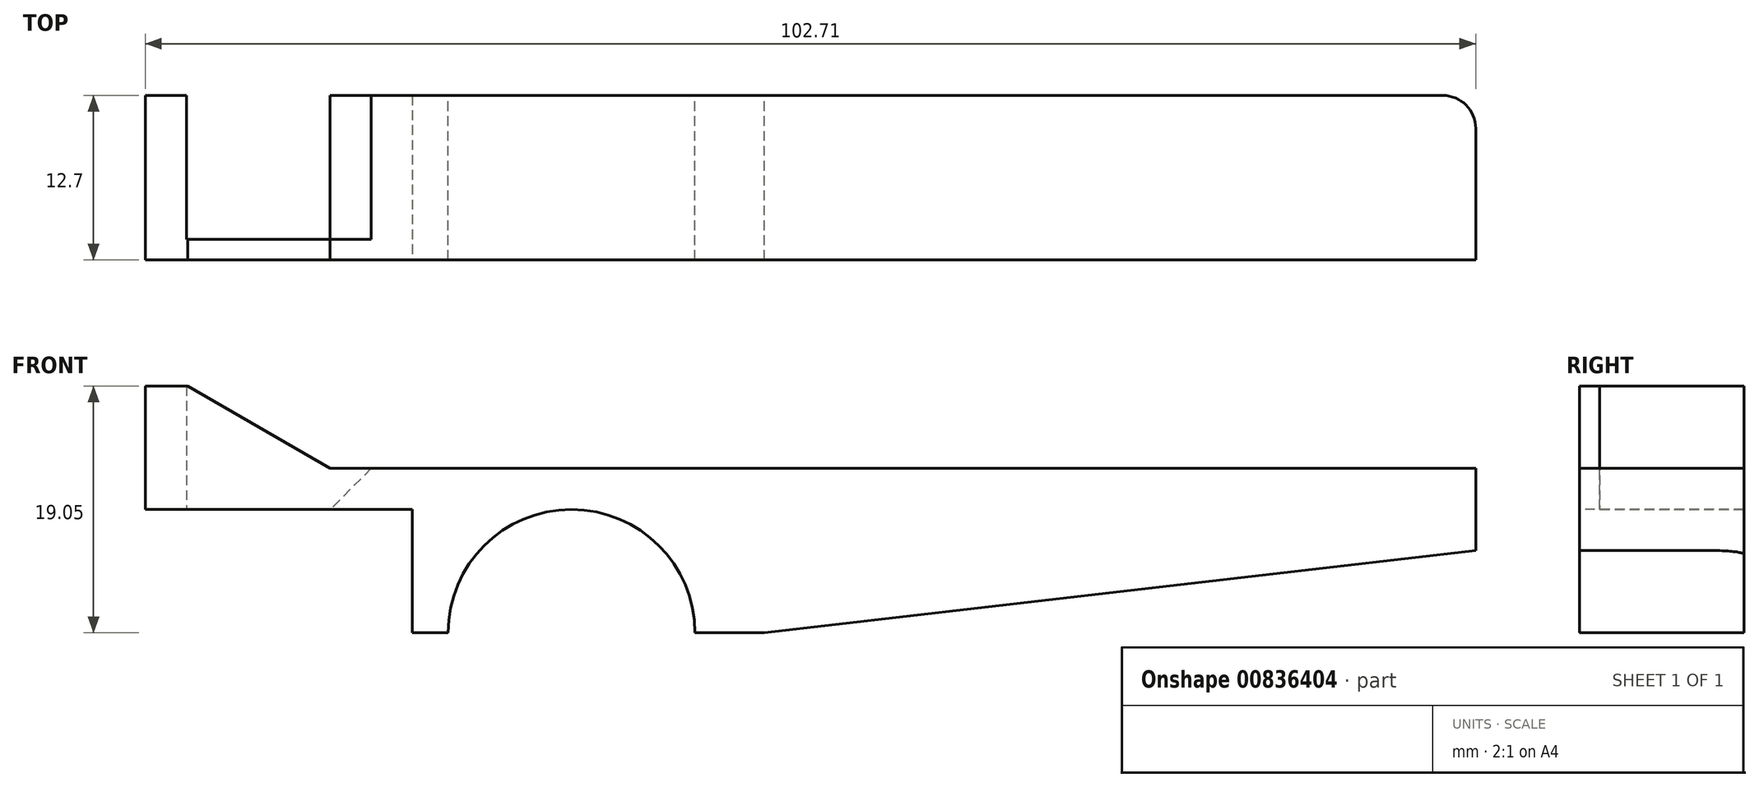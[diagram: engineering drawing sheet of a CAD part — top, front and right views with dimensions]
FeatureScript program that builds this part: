
annotation { "Feature Type Name" : "Feature", "Feature Type Description" : "" }
export const myFeature = defineFeature(function(context is Context, id is Id, definition is map)
    precondition{}
    {
        {
            var Q0;
            Q0=qCreatedBy(makeId("Top.planeOp"),FACE);
            var sketch = newSketch(context, id + "F0", { "sketchPlane" : qUnion([Q0])});
            skLineSegment(sketch, "E0.bottom", {"start": v(-19.03, 12.7) * mm, "end": v(19.07, 12.7) * mm});
            skLineSegment(sketch, "E0.top", {"start": v(-19.03, 0) * mm, "end": v(19.07, 0) * mm});
            skLineSegment(sketch, "E0.left", {"start": v(-19.03, 12.7) * mm, "end": v(-19.03, 0) * mm});
            skLineSegment(sketch, "E0.right", {"start": v(19.07, 12.7) * mm, "end": v(19.07, 0) * mm});
            skLineSegment(sketch, "E1.bottom", {"start": v(-19.03, 12.7) * mm, "end": v(-15.85, 12.7) * mm});
            skLineSegment(sketch, "E1.top", {"start": v(-19.03, 0) * mm, "end": v(-15.85, 0) * mm});
            skLineSegment(sketch, "E1.right", {"start": v(-15.85, 12.7) * mm, "end": v(-15.85, 0) * mm});
            skLineSegment(sketch, "E2.bottom", {"start": v(-15.85, 0) * mm, "end": v(-4.75, 0) * mm});
            skLineSegment(sketch, "E2.top", {"start": v(-15.85, 1.57) * mm, "end": v(-4.75, 1.57) * mm});
            skLineSegment(sketch, "E2.left", {"start": v(-15.85, 0) * mm, "end": v(-15.85, 1.57) * mm});
            skLineSegment(sketch, "E2.right", {"start": v(-4.75, 0) * mm, "end": v(-4.75, 1.57) * mm});
            skLineSegment(sketch, "E3.top", {"start": v(-15.85, 12.7) * mm, "end": v(-4.75, 12.7) * mm});
            skLineSegment(sketch, "E3.left", {"start": v(-15.85, 1.57) * mm, "end": v(-15.85, 12.7) * mm});
            skLineSegment(sketch, "E3.right", {"start": v(-4.75, 1.57) * mm, "end": v(-4.75, 12.7) * mm});
            skSolve(sketch);
        }
        {
            var Q0;
            {var subQ3=sQuery(id+"F0.wireOp",EDGE,"E0.right");Q0=makeQuery(id+"F0.imprint","IMPRINT",FACE,{"disambiguationData":[TD([[makeQuery(id+"F0.imprint","IMPRINT",EDGE,{"derivedFrom":subQ3}),-1.0]])]});}
            var Q1;
            {var subQ4=sQuery(id+"F0.wireOp",EDGE,"E0.left");Q1=makeQuery(id+"F0.imprint","IMPRINT",FACE,{"disambiguationData":[TD([[makeQuery(id+"F0.imprint","IMPRINT",EDGE,{"derivedFrom":subQ4}),1.0]])]});}
            var Q2;
            {var subQ4=sQuery(id+"F0.wireOp",EDGE,"E2.top");Q2=makeQuery(id+"F0.imprint","IMPRINT",FACE,{"disambiguationData":[TD([[makeQuery(id+"F0.imprint","IMPRINT",EDGE,{"derivedFrom":subQ4}),-1.0]])]});}
            extrude(context, id + "F1", {"entities" : qUnion([Q0, Q1, Q2]), "depth" : 12.7 * mm, "offsetDistance" : 25.4 * mm});
        }
        {
            var Q0;
            Q0=makeQuery(id+"F1.opExtrude","CAP_FACE",FACE,{"disambiguationData":[OSD([sQuery(id+"F0.wireOp",EDGE,"E0.bottom"),sQuery(id+"F0.wireOp",EDGE,"E0.top"),sQuery(id+"F0.wireOp",EDGE,"E0.left"),sQuery(id+"F0.wireOp",EDGE,"E0.right"),sQuery(id+"F0.wireOp",EDGE,"E1.right"),sQuery(id+"F0.wireOp",EDGE,"E2.top"),sQuery(id+"F0.wireOp",EDGE,"E3.right")])],"isStart":true});
            var sketch = newSketch(context, id + "F2", { "sketchPlane" : qUnion([Q0])});
            skLineSegment(sketch, "E4", {"start": v(-4.75, -1.57) * mm, "end": v(1.6, -1.57) * mm});
            skLineSegment(sketch, "E5", {"start": v(1.6, -1.57) * mm, "end": v(1.6, 0) * mm});
            skLineSegment(sketch, "E6", {"start": v(1.6, 0) * mm, "end": v(1.6, 0) * mm});
            skLineSegment(sketch, "E7", {"start": v(1.6, 0) * mm, "end": v(1.6, -12.7) * mm});
            skLineSegment(sketch, "E8", {"start": v(1.6, -12.7) * mm, "end": v(-19.03, -12.7) * mm});
            skLineSegment(sketch, "E9", {"start": v(-19.03, -12.7) * mm, "end": v(-19.03, 0) * mm});
            skLineSegment(sketch, "E10", {"start": v(-19.03, 0) * mm, "end": v(1.6, 0) * mm});
            skSolve(sketch);
        }
        {
            var Q0;
            Q0 = qSketchRegion(id + "F2", true);
            extrude(context, id + "F3", {"entities" : qUnion([Q0]), "operationType" : NewBodyOperationType.REMOVE, "oppositeDirection" : true, "depth" : 9.52 * mm, "offsetDistance" : 25.4 * mm});
        }
        {
            var Q0;
            Q0=makeQuery(id+"F1.opExtrude","CAP_FACE",FACE,{"disambiguationData":[OSD([sQuery(id+"F0.wireOp",EDGE,"E0.bottom"),sQuery(id+"F0.wireOp",EDGE,"E0.top"),sQuery(id+"F0.wireOp",EDGE,"E0.left"),sQuery(id+"F0.wireOp",EDGE,"E0.right"),sQuery(id+"F0.wireOp",EDGE,"E1.right"),sQuery(id+"F0.wireOp",EDGE,"E2.top"),sQuery(id+"F0.wireOp",EDGE,"E3.right")])],"isStart":false});
            var sketch = newSketch(context, id + "F4", { "sketchPlane" : qUnion([Q0])});
            skLineSegment(sketch, "E11", {"start": v(-19.03, 12.7) * mm, "end": v(-15.85, 12.7) * mm});
            skLineSegment(sketch, "E12", {"start": v(-15.85, 12.7) * mm, "end": v(-15.85, 1.57) * mm});
            skLineSegment(sketch, "E13", {"start": v(-15.85, 1.57) * mm, "end": v(-4.75, 1.57) * mm});
            skLineSegment(sketch, "E14", {"start": v(-4.75, 1.57) * mm, "end": v(-4.75, 0) * mm});
            skLineSegment(sketch, "E15", {"start": v(-4.75, 0) * mm, "end": v(-19.03, 0) * mm});
            skLineSegment(sketch, "E16", {"start": v(-19.03, 0) * mm, "end": v(-19.03, 12.7) * mm});
            skSolve(sketch);
        }
        {
            var Q0;
            Q0=makeQuery(id+"F4.imprint","IMPRINT",FACE,{"disambiguationData":[TD([[makeQuery(id+"F4.imprint","IMPRINT",EDGE,{"derivedFrom":sQuery(id+"F4.wireOp",EDGE,"E11")}),-1.0]])]});
            extrude(context, id + "F5", {"entities" : qUnion([Q0]), "operationType" : NewBodyOperationType.ADD, "depth" : 6.35 * mm, "offsetDistance" : 25.4 * mm});
        }
        {
            var Q0;
            Q0=makeQuery(id+"F5.opExtrude","CAP_EDGE",EDGE,{"disambiguationData":[OSD([sQuery(id+"F4.wireOp",EDGE,"E14")])],"isStart":false});
            chamfer(context, id + "F6", {"entities" : qUnion([Q0]), "chamferType" : ChamferType.OFFSET_ANGLE, "width" : 6.35 * mm, "oppositeDirection" : false, "angle" : 60 * degree, "tangentPropagation" : true});
        }
        {
            var Q0;
            Q0=makeQuery(id+"F1.opExtrude","CAP_EDGE",EDGE,{"disambiguationData":[OSD([sQuery(id+"F0.wireOp",EDGE,"E3.right")])],"isStart":false});
            chamfer(context, id + "F7", {"entities" : qUnion([Q0]), "width" : 3.17 * mm, "tangentPropagation" : true});
        }
        {
            var Q0;
            Q0=makeQuery(id+"F1.opExtrude","CAP_EDGE",EDGE,{"disambiguationData":[OSD([sQuery(id+"F0.wireOp",EDGE,"E0.right")])],"isStart":false});
            var Q1;
            Q1=makeQuery(id+"F1.opExtrude","CAP_EDGE",EDGE,{"disambiguationData":[OSD([sQuery(id+"F0.wireOp",EDGE,"E0.right")])],"isStart":true});
            var Q2;
            Q2=makeQuery(id+"F1.opExtrude","SWEPT_EDGE",EDGE,{"disambiguationData":[OSD([sQuery(id+"F0.wireOp",EDGE,"E0.bottom"),sQuery(id+"F0.wireOp",EDGE,"E0.right")])]});
            chamfer(context, id + "F8", {"entities" : qUnion([Q0, Q1, Q2]), "width" : 2.54 * mm, "tangentPropagation" : true});
        }
        {
            var Q0;
            Q0=makeQuery(id+"F1.opExtrude","CAP_FACE",FACE,{"disambiguationData":[OSD([sQuery(id+"F0.wireOp",EDGE,"E0.bottom"),sQuery(id+"F0.wireOp",EDGE,"E0.top"),sQuery(id+"F0.wireOp",EDGE,"E0.left"),sQuery(id+"F0.wireOp",EDGE,"E0.right"),sQuery(id+"F0.wireOp",EDGE,"E1.right"),sQuery(id+"F0.wireOp",EDGE,"E2.top"),sQuery(id+"F0.wireOp",EDGE,"E3.right")])],"isStart":false});
            var sketch = newSketch(context, id + "F9", { "sketchPlane" : qUnion([Q0])});
            skLineSegment(sketch, "E17.bottom", {"start": v(7.48, 12.7) * mm, "end": v(22.53, 12.7) * mm});
            skLineSegment(sketch, "E17.top", {"start": v(7.48, 0) * mm, "end": v(22.53, 0) * mm});
            skLineSegment(sketch, "E17.left", {"start": v(7.48, 12.7) * mm, "end": v(7.48, 0) * mm});
            skLineSegment(sketch, "E17.right", {"start": v(22.53, 12.7) * mm, "end": v(22.53, 0) * mm});
            skSolve(sketch);
        }
        {
            var Q0;
            Q0 = qSketchRegion(id + "F9", true);
            extrude(context, id + "F10", {"entities" : qUnion([Q0]), "operationType" : NewBodyOperationType.REMOVE, "oppositeDirection" : true, "depth" : 25.4 * mm, "offsetDistance" : 25.4 * mm});
        }
        {
            var Q0;
            Q0=makeQuery(id+"F10.boolean.opBoolean","COPY",FACE,{"derivedFrom":makeQuery(id+"F10.opExtrude","SWEPT_FACE",FACE,{"disambiguationData":[OSD([sQuery(id+"F9.wireOp",EDGE,"E17.left")])]})});
            extrude(context, id + "F11", {"entities" : qUnion([Q0]), "operationType" : NewBodyOperationType.ADD, "depth" : 76.2 * mm, "offsetDistance" : 25.4 * mm});
        }
        {
            var Q0;
            {var subQ0=sQuery(id+"F0.wireOp",EDGE,"E0.bottom");Q0=makeQuery(id+"F11.boolean.opBoolean","MERGE",FACE,{"derivedFrom":[makeQuery(id+"F1.opExtrude","SWEPT_FACE",FACE,{"disambiguationData":[OSD([subQ0]),TDD([makeQuery(id+"F0.imprint","IMPRINT",EDGE,{"disambiguationData":[TD([[makeQuery(id+"F0.imprint","INTERSECT",VERTEX,{"derivedFrom":[subQ0,sQuery(id+"F0.wireOp",EDGE,"E3.right")]}),-1.0]])],"derivedFrom":subQ0})])]}),makeQuery(id+"F11.opExtrude","SWEPT_FACE",FACE,{"disambiguationData":[OSD([subQ0,sQuery(id+"F9.wireOp",EDGE,"E17.bottom"),sQuery(id+"F9.wireOp",EDGE,"E17.left")])]})]});}
            var sketch = newSketch(context, id + "F12", { "sketchPlane" : qUnion([Q0])});
            skPoint(sketch, "E18", {"position": v(-13.88, 0) * mm});
            skCircle(sketch, "E19", {"center": v(-13.88, 0) * mm, "radius": 9.53 * mm});
            skSolve(sketch);
        }
        {
            var Q0;
            {var subQ0=sQuery(id+"F12.wireOp",EDGE,"E19");var subQ1=sQuery(id+"F9.wireOp",EDGE,"E17.left");var subQ2=sQuery(id+"F0.wireOp",EDGE,"E3.right");var subQ3=sQuery(id+"F0.wireOp",EDGE,"E2.top");var subQ4=sQuery(id+"F0.wireOp",EDGE,"E1.right");var subQ5=sQuery(id+"F0.wireOp",EDGE,"E0.right");var subQ6=sQuery(id+"F0.wireOp",EDGE,"E0.left");var subQ7=sQuery(id+"F0.wireOp",EDGE,"E0.top");var subQ8=sQuery(id+"F0.wireOp",EDGE,"E0.bottom");var subQ9=makeQuery(id+"F11.boolean.opBoolean","MERGE",EDGE,{"derivedFrom":[makeQuery(id+"F1.opExtrude","CAP_EDGE",EDGE,{"disambiguationData":[OSD([subQ8]),TDD([makeQuery(id+"F0.imprint","IMPRINT",EDGE,{"disambiguationData":[TD([[makeQuery(id+"F0.imprint","INTERSECT",VERTEX,{"derivedFrom":[subQ8,subQ2]}),-1.0]])],"derivedFrom":subQ8})])],"isStart":true}),makeQuery(id+"F11.opExtrude","SWEPT_EDGE",EDGE,{"disambiguationData":[OSD([subQ8,subQ7,subQ6,subQ5,subQ4,subQ3,subQ2,subQ1]),TDD([makeQuery(id+"F10.boolean.opBoolean","INTERSECT",VERTEX,{"disambiguationData":[OD(0.0)],"derivedFrom":[makeQuery(id+"F1.opExtrude","CAP_FACE",FACE,{"disambiguationData":[OSD([subQ8,subQ7,subQ6,subQ5,subQ4,subQ3,subQ2])],"isStart":true}),makeQuery(id+"F10.opExtrude","SWEPT_FACE",FACE,{"disambiguationData":[OSD([subQ1])]})]})])]})]});var subQ10=makeQuery(id+"F12.imprint","INTERSECT",VERTEX,{"disambiguationData":[OD(0.0)],"derivedFrom":[subQ9,subQ0]});Q0=makeQuery(id+"F12.imprint","IMPRINT",FACE,{"disambiguationData":[TD([[makeQuery(id+"F12.imprint","IMPRINT",EDGE,{"disambiguationData":[TD([[subQ10,-1.0]])],"derivedFrom":subQ0}),1.0]])]});}
            extrude(context, id + "F13", {"entities" : qUnion([Q0]), "operationType" : NewBodyOperationType.REMOVE, "oppositeDirection" : true, "depth" : 25.4 * mm, "offsetDistance" : 25.4 * mm});
        }
        {
            var Q0;
            {var subQ0=sQuery(id+"F0.wireOp",EDGE,"E0.bottom");Q0=makeQuery(id+"F11.boolean.opBoolean","MERGE",FACE,{"derivedFrom":[makeQuery(id+"F1.opExtrude","SWEPT_FACE",FACE,{"disambiguationData":[OSD([subQ0]),TDD([makeQuery(id+"F0.imprint","IMPRINT",EDGE,{"disambiguationData":[TD([[makeQuery(id+"F0.imprint","INTERSECT",VERTEX,{"derivedFrom":[subQ0,sQuery(id+"F0.wireOp",EDGE,"E3.right")]}),-1.0]])],"derivedFrom":subQ0})])]}),makeQuery(id+"F11.opExtrude","SWEPT_FACE",FACE,{"disambiguationData":[OSD([subQ0,sQuery(id+"F9.wireOp",EDGE,"E17.bottom"),sQuery(id+"F9.wireOp",EDGE,"E17.left")])]})]});}
            var sketch = newSketch(context, id + "F14", { "sketchPlane" : qUnion([Q0])});
            skLineSegment(sketch, "E20", {"start": v(-28.77, 0) * mm, "end": v(-83.68, 6.35) * mm});
            skSolve(sketch);
        }
        {
            var Q0;
            {var subQ0=sQuery(id+"F14.wireOp",EDGE,"E20");Q0=makeQuery(id+"F14.imprint","IMPRINT",FACE,{"disambiguationData":[TD([[makeQuery(id+"F14.imprint","IMPRINT",EDGE,{"derivedFrom":subQ0}),1.0]])]});}
            extrude(context, id + "F15", {"entities" : qUnion([Q0]), "operationType" : NewBodyOperationType.REMOVE, "oppositeDirection" : true, "depth" : 25.4 * mm, "offsetDistance" : 25.4 * mm});
        }
        {
            var Q0;
            Q0=makeQuery(id+"F11.opExtrude","CAP_EDGE",EDGE,{"disambiguationData":[OSD([sQuery(id+"F9.wireOp",EDGE,"E17.left")])],"isStart":false});
            var Q1;
            Q1=makeQuery(id+"F15.boolean.opBoolean","COPY",EDGE,{"derivedFrom":makeQuery(id+"F15.opExtrude","SWEPT_EDGE",EDGE,{"disambiguationData":[OSD([sQuery(id+"F0.wireOp",EDGE,"E0.bottom"),sQuery(id+"F9.wireOp",EDGE,"E17.bottom"),sQuery(id+"F9.wireOp",EDGE,"E17.left"),sQuery(id+"F14.wireOp",EDGE,"E20")])]})});
            fillet(context, id + "F16", {"entities" : qUnion([Q0, Q1]), "radius" : 2.54 * mm, "tangentPropagation" : true, "allowEdgeOverflow" : false});
        }
    });
